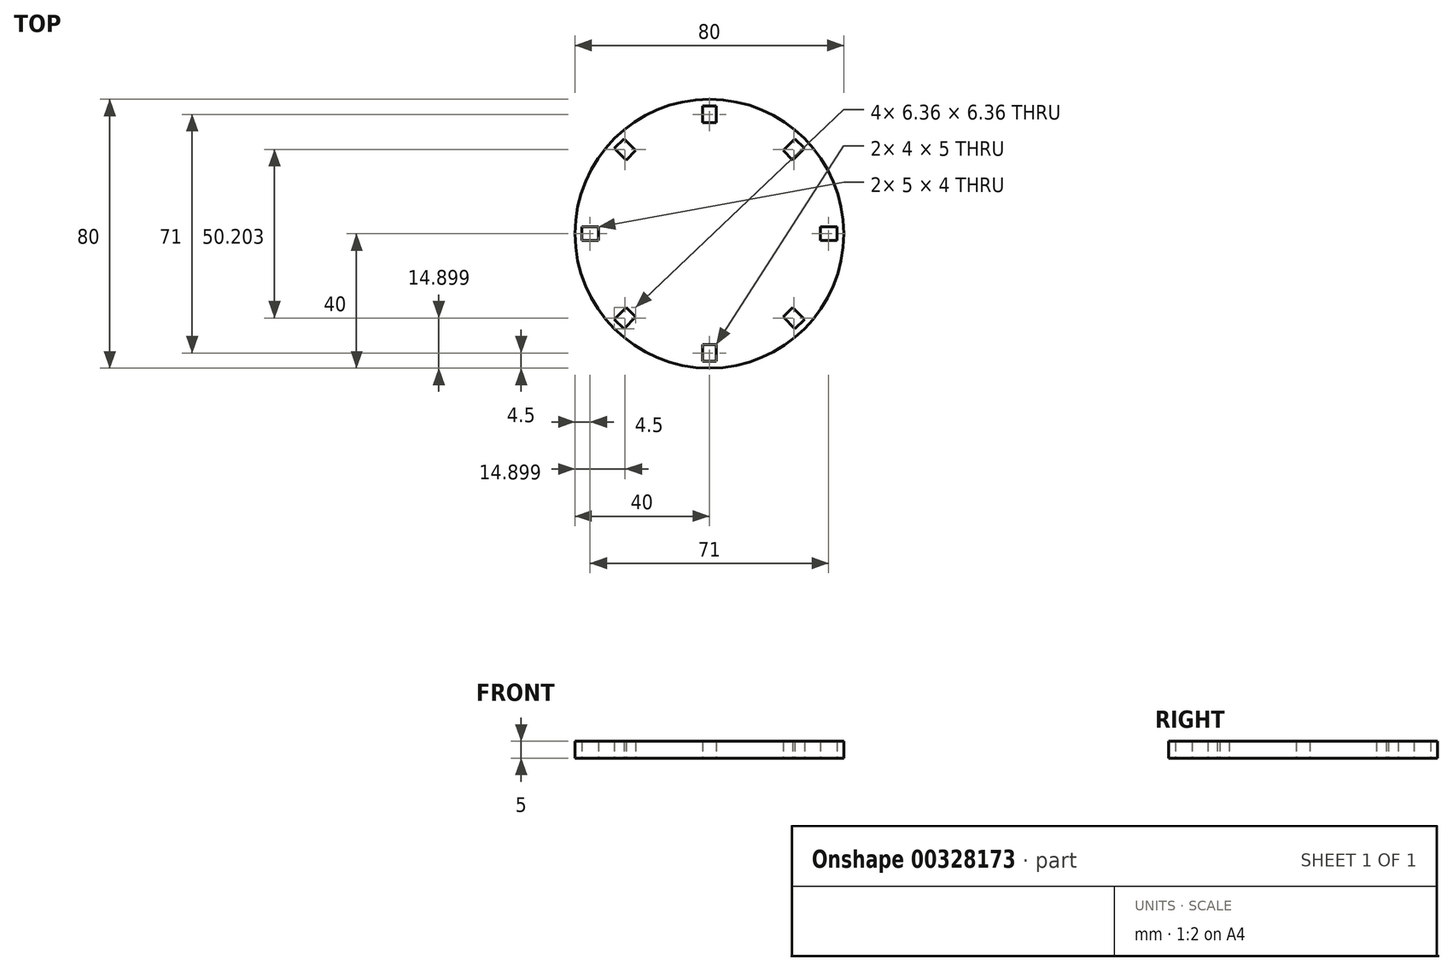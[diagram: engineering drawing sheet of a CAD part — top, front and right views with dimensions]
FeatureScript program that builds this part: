
annotation { "Feature Type Name" : "Feature", "Feature Type Description" : "" }
export const myFeature = defineFeature(function(context is Context, id is Id, definition is map)
    precondition{}
    {
        {
            var Q0;
            Q0=qCreatedBy(makeId("Top.planeOp"),FACE);
            var sketch = newSketch(context, id + "F0", { "sketchPlane" : qUnion([Q0])});
            skCircle(sketch, "E0", {"center": v(0, 0) * mm, "radius": 40 * mm});
            skLineSegment(sketch, "E1", {"start": v(-40, 0) * mm, "end": v(40, 0) * mm, "construction": true});
            skLineSegment(sketch, "E2", {"start": v(40, 0) * mm, "end": v(38, 0) * mm, "construction": true});
            skLineSegment(sketch, "E3", {"start": v(-40, 0) * mm, "end": v(-38, 0) * mm, "construction": true});
            skLineSegment(sketch, "E4", {"start": v(-38, 0) * mm, "end": v(-33, 0) * mm, "construction": true});
            skLineSegment(sketch, "E5", {"start": v(-38, 0) * mm, "end": v(-38, 2) * mm});
            skLineSegment(sketch, "E6", {"start": v(-38, 2) * mm, "end": v(-33, 2) * mm});
            skLineSegment(sketch, "E7", {"start": v(-33, 2) * mm, "end": v(-33, -2) * mm});
            skLineSegment(sketch, "E8", {"start": v(-33, -2) * mm, "end": v(-38, -2) * mm});
            skLineSegment(sketch, "E9", {"start": v(-38, -2) * mm, "end": v(-38, 0) * mm});
            skLineSegment(sketch, "E10", {"start": v(0, -40) * mm, "end": v(0, -38) * mm, "construction": true});
            skLineSegment(sketch, "E11", {"start": v(0, -38) * mm, "end": v(2, -38) * mm});
            skLineSegment(sketch, "E12", {"start": v(2, -38) * mm, "end": v(2, -33) * mm});
            skLineSegment(sketch, "E13", {"start": v(2, -33) * mm, "end": v(-2, -33) * mm});
            skLineSegment(sketch, "E14", {"start": v(-2, -33) * mm, "end": v(-2, -38) * mm});
            skLineSegment(sketch, "E15", {"start": v(-2, -38) * mm, "end": v(0, -38) * mm});
            skLineSegment(sketch, "E16", {"start": v(0, 40) * mm, "end": v(0, 38) * mm, "construction": true});
            skLineSegment(sketch, "E17", {"start": v(0, 38) * mm, "end": v(2, 38) * mm});
            skLineSegment(sketch, "E18", {"start": v(2, 38) * mm, "end": v(2, 33) * mm});
            skLineSegment(sketch, "E19", {"start": v(2, 33) * mm, "end": v(-2, 33) * mm});
            skLineSegment(sketch, "E20", {"start": v(-2, 33) * mm, "end": v(-2, 38) * mm});
            skLineSegment(sketch, "E21", {"start": v(-2, 38) * mm, "end": v(0, 38) * mm});
            skLineSegment(sketch, "E22", {"start": v(38, 0) * mm, "end": v(38, 2) * mm});
            skLineSegment(sketch, "E23", {"start": v(38, 2) * mm, "end": v(33, 2) * mm});
            skLineSegment(sketch, "E24", {"start": v(33, 2) * mm, "end": v(33, -2) * mm});
            skLineSegment(sketch, "E25", {"start": v(33, -2) * mm, "end": v(38, -2) * mm});
            skLineSegment(sketch, "E26", {"start": v(38, -2) * mm, "end": v(38, 0) * mm});
            skLineSegment(sketch, "E27", {"start": v(2, 33) * mm, "end": v(33, 2) * mm, "construction": true});
            skLineSegment(sketch, "E28", {"start": v(17.5, 17.5) * mm, "end": v(23.33, 23.33) * mm, "construction": true});
            skLineSegment(sketch, "E29", {"start": v(23.33, 23.33) * mm, "end": v(24.75, 21.92) * mm});
            skLineSegment(sketch, "E30", {"start": v(24.75, 21.92) * mm, "end": v(28.28, 25.45) * mm});
            skLineSegment(sketch, "E31", {"start": v(28.28, 25.45) * mm, "end": v(25.45, 28.28) * mm});
            skLineSegment(sketch, "E32", {"start": v(25.45, 28.28) * mm, "end": v(21.92, 24.75) * mm});
            skLineSegment(sketch, "E33", {"start": v(21.92, 24.75) * mm, "end": v(23.33, 23.33) * mm});
            skLineSegment(sketch, "E34", {"start": v(2, -33) * mm, "end": v(33, -2) * mm, "construction": true});
            skLineSegment(sketch, "E35", {"start": v(17.5, -17.5) * mm, "end": v(23.33, -23.33) * mm, "construction": true});
            skLineSegment(sketch, "E36", {"start": v(23.33, -23.33) * mm, "end": v(24.75, -21.92) * mm});
            skLineSegment(sketch, "E37", {"start": v(24.75, -21.92) * mm, "end": v(28.28, -25.45) * mm});
            skLineSegment(sketch, "E38", {"start": v(28.28, -25.45) * mm, "end": v(25.45, -28.28) * mm});
            skLineSegment(sketch, "E39", {"start": v(25.45, -28.28) * mm, "end": v(21.92, -24.75) * mm});
            skLineSegment(sketch, "E40", {"start": v(21.92, -24.75) * mm, "end": v(23.33, -23.33) * mm});
            skLineSegment(sketch, "E41", {"start": v(-33, -2) * mm, "end": v(-2, -33) * mm, "construction": true});
            skLineSegment(sketch, "E42", {"start": v(-17.5, -17.5) * mm, "end": v(-23.33, -23.33) * mm, "construction": true});
            skLineSegment(sketch, "E43", {"start": v(-23.33, -23.33) * mm, "end": v(-21.92, -24.75) * mm});
            skLineSegment(sketch, "E44", {"start": v(-21.92, -24.75) * mm, "end": v(-25.45, -28.28) * mm});
            skLineSegment(sketch, "E45", {"start": v(-25.45, -28.28) * mm, "end": v(-28.28, -25.45) * mm});
            skLineSegment(sketch, "E46", {"start": v(-28.28, -25.45) * mm, "end": v(-24.75, -21.92) * mm});
            skLineSegment(sketch, "E47", {"start": v(-24.75, -21.92) * mm, "end": v(-23.33, -23.33) * mm});
            skLineSegment(sketch, "E48", {"start": v(-33, 2) * mm, "end": v(-2, 33) * mm, "construction": true});
            skLineSegment(sketch, "E49", {"start": v(-17.5, 17.5) * mm, "end": v(-23.33, 23.33) * mm, "construction": true});
            skLineSegment(sketch, "E50", {"start": v(-23.33, 23.33) * mm, "end": v(-24.75, 21.92) * mm});
            skLineSegment(sketch, "E51", {"start": v(-24.75, 21.92) * mm, "end": v(-28.28, 25.45) * mm});
            skLineSegment(sketch, "E52", {"start": v(-28.28, 25.45) * mm, "end": v(-25.45, 28.28) * mm});
            skLineSegment(sketch, "E53", {"start": v(-25.45, 28.28) * mm, "end": v(-21.92, 24.75) * mm});
            skLineSegment(sketch, "E54", {"start": v(-21.92, 24.75) * mm, "end": v(-23.33, 23.33) * mm});
            skSolve(sketch);
        }
        {
            var Q0;
            Q0=makeQuery(id+"F0.imprint","IMPRINT",FACE,{"disambiguationData":[TD([[makeQuery(id+"F0.imprint","IMPRINT",EDGE,{"derivedFrom":sQuery(id+"F0.wireOp",EDGE,"E0")}),1.0]])]});
            extrude(context, id + "F1", {"entities" : qUnion([Q0]), "depth" : 5 * mm});
        }
    });
